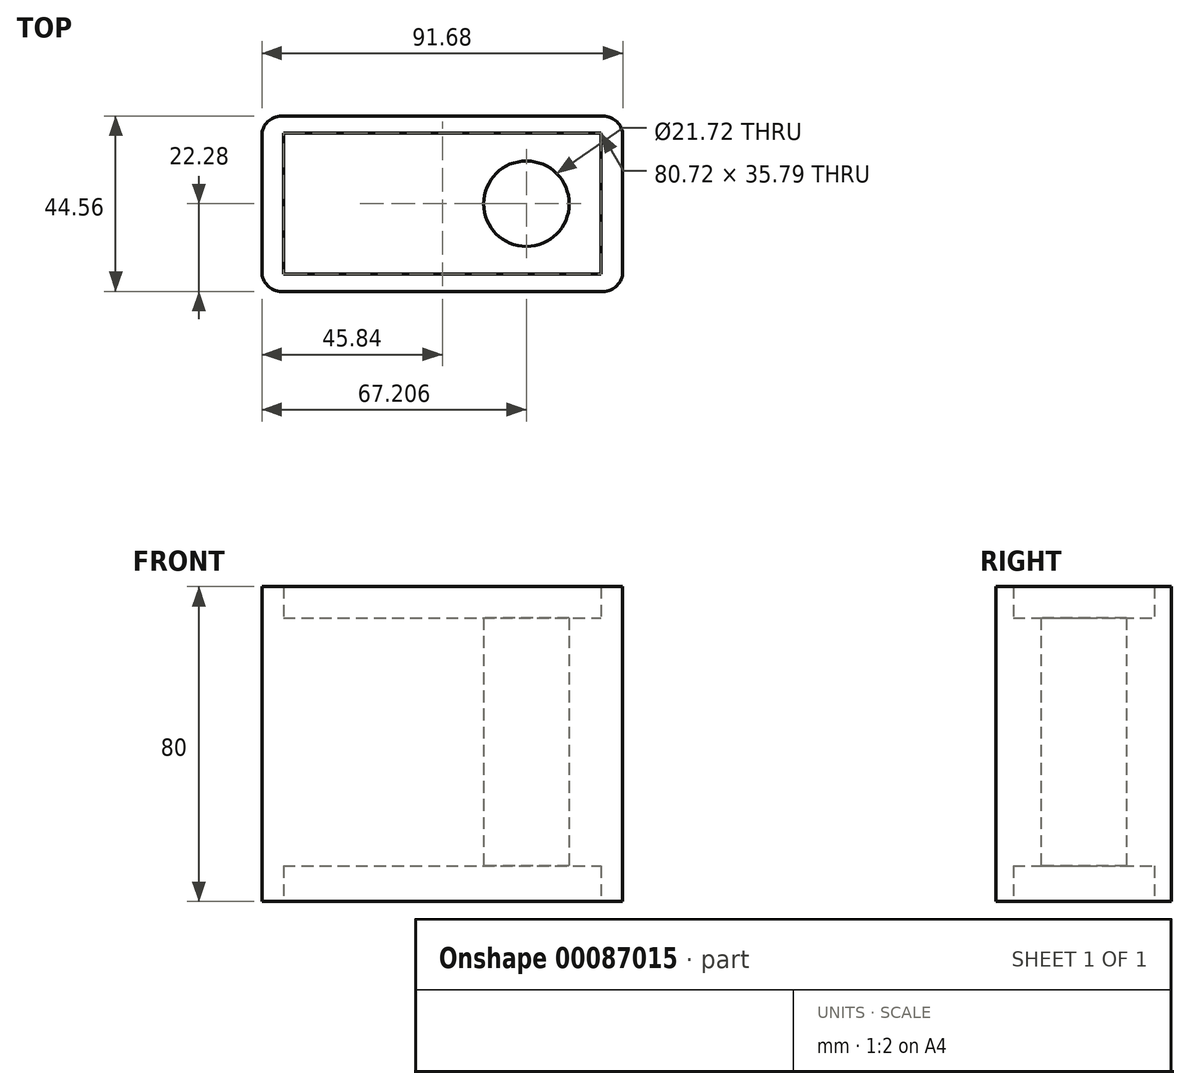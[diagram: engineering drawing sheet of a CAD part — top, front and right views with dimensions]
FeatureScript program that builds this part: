
annotation { "Feature Type Name" : "Feature", "Feature Type Description" : "" }
export const myFeature = defineFeature(function(context is Context, id is Id, definition is map)
    precondition{}
    {
        {
            var Q0;
            Q0=qCreatedBy(makeId("Top.planeOp"),FACE);
            var sketch = newSketch(context, id + "F0", { "sketchPlane" : qUnion([Q0])});
            skLineSegment(sketch, "E0.bottom", {"start": v(-45.84, -22.28) * mm, "end": v(45.84, -22.28) * mm});
            skLineSegment(sketch, "E0.top", {"start": v(-45.84, 22.28) * mm, "end": v(45.84, 22.28) * mm});
            skLineSegment(sketch, "E0.left", {"start": v(-45.84, -22.28) * mm, "end": v(-45.84, 22.28) * mm});
            skLineSegment(sketch, "E0.right", {"start": v(45.84, -22.28) * mm, "end": v(45.84, 22.28) * mm});
            skPoint(sketch, "E0.middle", {"position": v(0, 0) * mm});
            skLineSegment(sketch, "E1.bottom", {"start": v(-40.36, -17.9) * mm, "end": v(40.36, -17.9) * mm});
            skLineSegment(sketch, "E1.top", {"start": v(-40.36, 17.9) * mm, "end": v(40.36, 17.9) * mm});
            skLineSegment(sketch, "E1.left", {"start": v(-40.36, -17.9) * mm, "end": v(-40.36, 17.9) * mm});
            skLineSegment(sketch, "E1.right", {"start": v(40.36, -17.9) * mm, "end": v(40.36, 17.9) * mm});
            skCircle(sketch, "E2", {"center": v(21.37, 0) * mm, "radius": 10.86 * mm});
            skSolve(sketch);
        }
        {
            var Q0;
            Q0=makeQuery(id+"F0.imprint","IMPRINT",FACE,{"disambiguationData":[TD([[makeQuery(id+"F0.imprint","IMPRINT",EDGE,{"derivedFrom":sQuery(id+"F0.wireOp",EDGE,"E0.bottom")}),1.0]])]});
            extrude(context, id + "F1", {"entities" : qUnion([Q0]), "depth" : 80 * mm});
        }
        {
            var Q0;
            Q0=makeQuery(id+"F0.imprint","IMPRINT",FACE,{"disambiguationData":[TD([[makeQuery(id+"F0.imprint","IMPRINT",EDGE,{"derivedFrom":sQuery(id+"F0.wireOp",EDGE,"E1.bottom")}),1.0]])]});
            extrude(context, id + "F2", {"entities" : qUnion([Q0]), "operationType" : NewBodyOperationType.ADD, "depth" : 72 * mm, "hasSecondDirection" : true, "secondDirectionOppositeDirection" : false, "secondDirectionDepth" : 9 * mm});
        }
        {
            var Q0;
            Q0=makeQuery(id+"F1.opExtrude","SWEPT_EDGE",EDGE,{"disambiguationData":[OSD([sQuery(id+"F0.wireOp",EDGE,"E0.bottom"),sQuery(id+"F0.wireOp",EDGE,"E0.right")])]});
            var Q1;
            Q1=makeQuery(id+"F1.opExtrude","SWEPT_EDGE",EDGE,{"disambiguationData":[OSD([sQuery(id+"F0.wireOp",EDGE,"E0.top"),sQuery(id+"F0.wireOp",EDGE,"E0.right")])]});
            var Q2;
            Q2=makeQuery(id+"F1.opExtrude","SWEPT_EDGE",EDGE,{"disambiguationData":[OSD([sQuery(id+"F0.wireOp",EDGE,"E0.top"),sQuery(id+"F0.wireOp",EDGE,"E0.left")])]});
            var Q3;
            Q3=makeQuery(id+"F1.opExtrude","SWEPT_EDGE",EDGE,{"disambiguationData":[OSD([sQuery(id+"F0.wireOp",EDGE,"E0.bottom"),sQuery(id+"F0.wireOp",EDGE,"E0.left")])]});
            fillet(context, id + "F3", {"entities" : qUnion([Q0, Q1, Q2, Q3]), "radius" : 5 * mm, "tangentPropagation" : true, "allowEdgeOverflow" : false});
        }
    });
